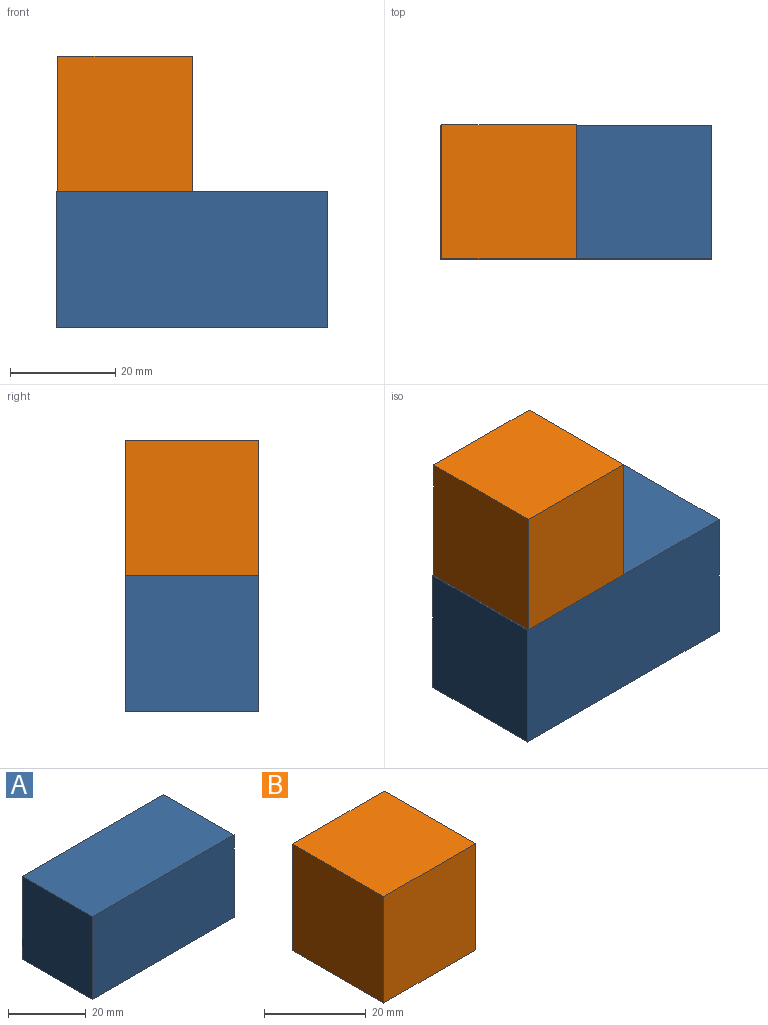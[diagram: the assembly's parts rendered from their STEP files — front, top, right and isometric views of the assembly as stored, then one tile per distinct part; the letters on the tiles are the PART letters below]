
ASSEMBLY  parts=2 mates=1
PART A: 6 faces, bbox 51.5x25.4x26 mm
  f0: plane 51.49x25.4mm, normal (0,0,1), area 1307.9mm2, adj f1,f3,f4,f5
  f1: plane 25.97x25.4mm, normal (-1,0,0), area 659.7mm2, adj f0,f2,f4,f5
  f2: plane 51.49x25.4mm, normal (0,0,-1), area 1307.9mm2, adj f1,f3,f4,f5
  f3: plane 25.97x25.4mm, normal (1,0,0), area 659.7mm2, adj f0,f2,f4,f5
  f4: plane 51.49x25.97mm, normal (0,-1,0), area 1337.4mm2, adj f0,f1,f2,f3
  f5: plane 51.49x25.97mm, normal (0,1,0), area 1337.4mm2, adj f0,f1,f2,f3
PART B: 6 faces, bbox 25.6x25.4x25.6 mm
  f0: plane 25.57x25.4mm, normal (0,0,1), area 649.4mm2, adj f1,f3,f4,f5
  f1: plane 25.65x25.4mm, normal (-1,0,0), area 651.4mm2, adj f0,f2,f4,f5
  f2: plane 25.57x25.4mm, normal (0,0,-1), area 649.4mm2, adj f1,f3,f4,f5
  f3: plane 25.65x25.4mm, normal (1,0,0), area 651.4mm2, adj f0,f2,f4,f5
  f4: plane 25.65x25.57mm, normal (0,-1,0), area 655.7mm2, adj f0,f1,f2,f3
  f5: plane 25.65x25.57mm, normal (0,1,0), area 655.7mm2, adj f0,f1,f2,f3
PLACE A t=(50.59,-12.94,20)mm
PLACE B t=(50.14,-12.94,14.55)mm
MATE fastened B.f2 <-> A.f0  axis (0,0,-1) through (-68.38,-25.64,7.2)mm
